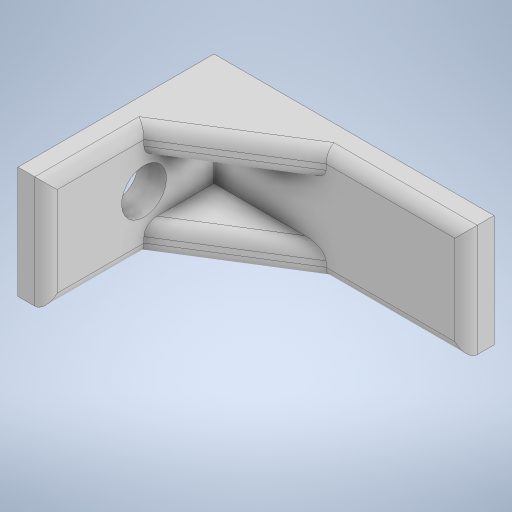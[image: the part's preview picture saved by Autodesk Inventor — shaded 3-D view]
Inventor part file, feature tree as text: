
AUTODESK INVENTOR PART (.ipt)
format: ipt  version: 2024.2 (Build 282272000, 272)  size: 283,136 bytes
history: native  units: mm
features: sketch x5, extrude x4, fillet x2, mirror x1, projected_geometry x1
ambient origin geometry x8: Origin, YZ Plane, XZ Plane, XY Plane, X Axis, Y Axis, Z Axis, Center Point
bodies: Solid1 (feature_tree)
feature tree (13):
  extrude  "Extrusion1"  Depth=20.0mm
  extrude  "Extrusion2"  Depth=5.0mm
  sketch  "Sketch3"  dims[d5=30.0mm d6=0.0mm d7=10.599979mm]
  extrude  "Extrusion3"  Depth=30.0mm
  mirror  "Mirror1"
  extrude  "Extrusion4"  Depth=10.0mm
  fillet  "Fillet1"  Radius=12.5mm
  fillet  "Fillet2"  Radius=10.0mm
  sketch  "Sketch1"  dims[d0=50.0mm d1=20.0mm]
  sketch  "Sketch2"  dims[d2=5.0mm d3=0.0mm d4=5.0mm]
  sketch  "Sketch4"  dims[d8=5.0mm d9=0.0mm d10=8.0mm d11=12.5mm d12=10.0mm]
  projected_geometry  "Projected Loop1"
  sketch  "Sketch5"  dims[d13=5.0mm d14=0.0mm d15=2.0mm d16=2.0mm]
